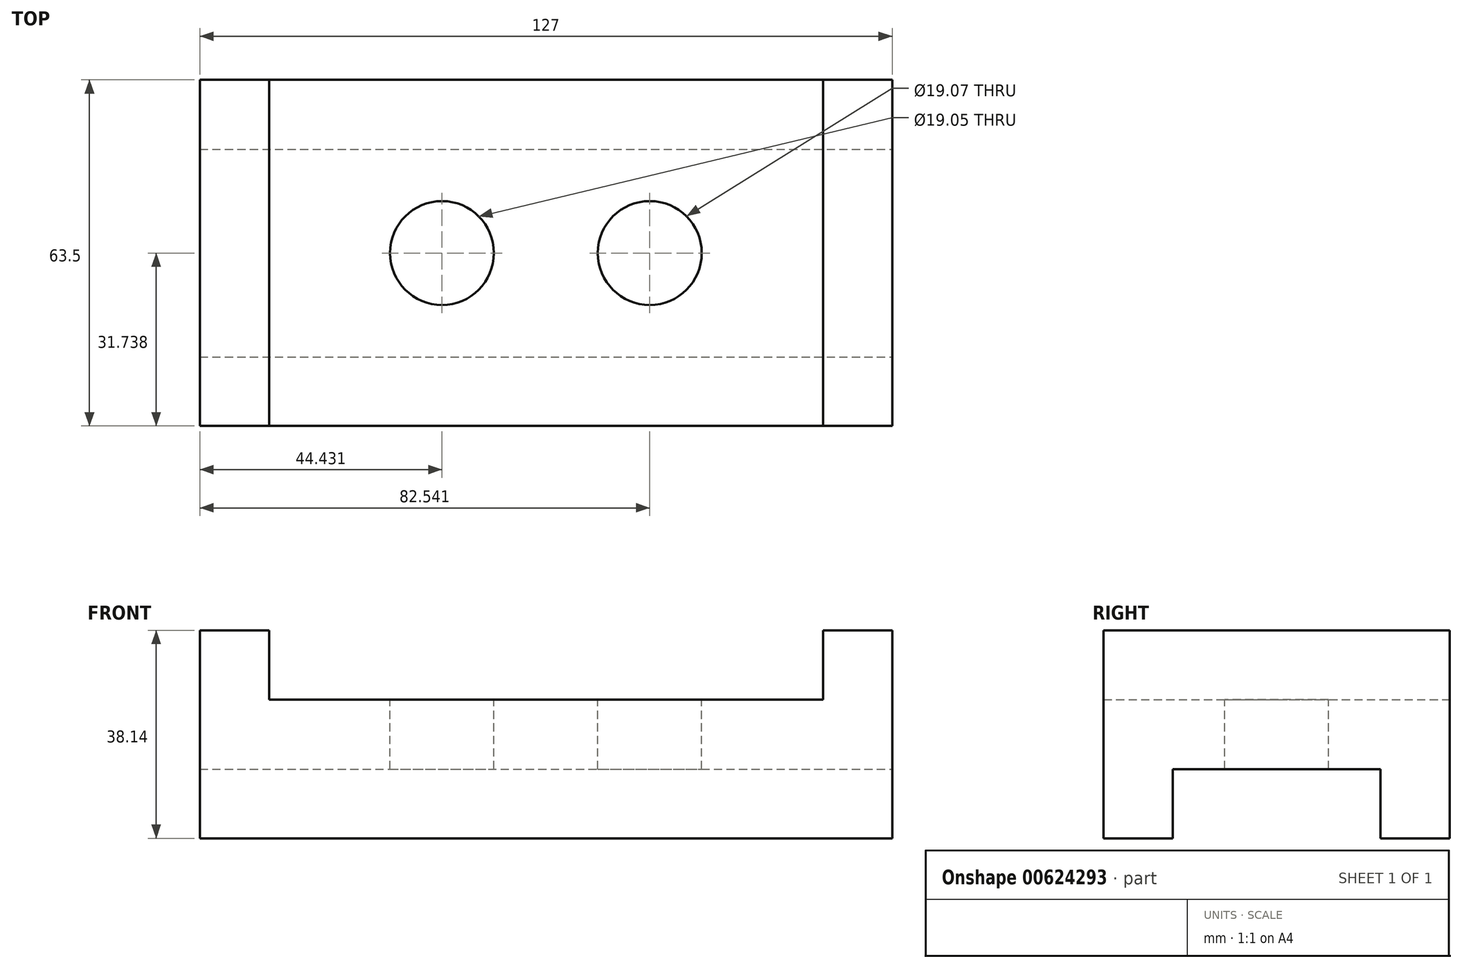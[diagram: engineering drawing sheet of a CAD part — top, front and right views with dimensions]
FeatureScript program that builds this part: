
annotation { "Feature Type Name" : "Feature", "Feature Type Description" : "" }
export const myFeature = defineFeature(function(context is Context, id is Id, definition is map)
    precondition{}
    {
        {
            var Q0;
            Q0=qCreatedBy(makeId("Front.planeOp"),FACE);
            var sketch = newSketch(context, id + "F0", { "sketchPlane" : qUnion([Q0])});
            skLineSegment(sketch, "E0", {"start": v(0, 0) * mm, "end": v(-63.5, 0) * mm});
            skLineSegment(sketch, "E1", {"start": v(-63.5, 0) * mm, "end": v(-63.5, 38.14) * mm});
            skLineSegment(sketch, "E2", {"start": v(-63.5, 38.14) * mm, "end": v(-50.8, 38.14) * mm});
            skLineSegment(sketch, "E3", {"start": v(-50.8, 38.14) * mm, "end": v(-50.8, 25.43) * mm});
            skLineSegment(sketch, "E4", {"start": v(-50.8, 25.43) * mm, "end": v(0, 25.43) * mm});
            skLineSegment(sketch, "E5.MirrorCS", {"start": v(63.5, 0) * mm, "end": v(63.5, 38.14) * mm});
            skLineSegment(sketch, "E6.MirrorCS", {"start": v(50.8, 25.43) * mm, "end": v(0, 25.43) * mm});
            skLineSegment(sketch, "E7.MirrorCS", {"start": v(0, 0) * mm, "end": v(63.5, 0) * mm});
            skLineSegment(sketch, "E8.MirrorCS", {"start": v(63.5, 38.14) * mm, "end": v(50.8, 38.14) * mm});
            skLineSegment(sketch, "E9.MirrorCS", {"start": v(50.8, 38.14) * mm, "end": v(50.8, 25.43) * mm});
            skSolve(sketch);
        }
        {
            var Q0;
            Q0=makeQuery(id+"F0.imprint","IMPRINT",FACE,{"disambiguationData":[TD([[makeQuery(id+"F0.imprint","IMPRINT",EDGE,{"derivedFrom":sQuery(id+"F0.wireOp",EDGE,"E0")}),-1.0]])]});
            extrude(context, id + "F1", {"entities" : qUnion([Q0]), "depth" : 63.5 * mm, "offsetDistance" : 25.4 * mm});
        }
        {
            var Q0;
            Q0=makeQuery(id+"F1.opExtrude","SWEPT_FACE",FACE,{"disambiguationData":[OSD([sQuery(id+"F0.wireOp",EDGE,"E5.MirrorCS")])]});
            var sketch = newSketch(context, id + "F2", { "sketchPlane" : qUnion([Q0])});
            skLineSegment(sketch, "E10", {"start": v(-50.81, 0) * mm, "end": v(-50.81, 12.7) * mm});
            skLineSegment(sketch, "E11", {"start": v(-50.81, 12.7) * mm, "end": v(-12.71, 12.7) * mm});
            skLineSegment(sketch, "E12", {"start": v(-12.71, 12.7) * mm, "end": v(-12.71, 0) * mm});
            skSolve(sketch);
        }
        {
            var Q0;
            {var subQ0=sQuery(id+"F2.wireOp",EDGE,"E10");Q0=makeQuery(id+"F2.imprint","IMPRINT",FACE,{"disambiguationData":[TD([[makeQuery(id+"F2.imprint","IMPRINT",EDGE,{"derivedFrom":subQ0}),-1.0]])]});}
            extrude(context, id + "F3", {"entities" : qUnion([Q0]), "operationType" : NewBodyOperationType.REMOVE, "oppositeDirection" : true, "depth" : 127 * mm, "offsetDistance" : 25.4 * mm});
        }
        {
            var Q0;
            Q0=makeQuery(id+"F1.opExtrude","SWEPT_FACE",FACE,{"disambiguationData":[OSD([sQuery(id+"F0.wireOp",EDGE,"E4"),sQuery(id+"F0.wireOp",EDGE,"E6.MirrorCS")])]});
            var sketch = newSketch(context, id + "F4", { "sketchPlane" : qUnion([Q0])});
            skCircle(sketch, "E13", {"center": v(-19.07, -31.76) * mm, "radius": 9.53 * mm});
            skCircle(sketch, "E14", {"center": v(19.04, -31.76) * mm, "radius": 9.53 * mm});
            skSolve(sketch);
        }
        {
            var Q0;
            Q0=makeQuery(id+"F4.imprint","IMPRINT",FACE,{"disambiguationData":[TD([[makeQuery(id+"F4.imprint","IMPRINT",EDGE,{"derivedFrom":sQuery(id+"F4.wireOp",EDGE,"E13")}),1.0]])]});
            var Q1;
            Q1=makeQuery(id+"F4.imprint","IMPRINT",FACE,{"disambiguationData":[TD([[makeQuery(id+"F4.imprint","IMPRINT",EDGE,{"derivedFrom":sQuery(id+"F4.wireOp",EDGE,"E14")}),1.0]])]});
            extrude(context, id + "F5", {"entities" : qUnion([Q0, Q1]), "operationType" : NewBodyOperationType.REMOVE, "oppositeDirection" : true, "depth" : 38.1 * mm, "offsetDistance" : 25.4 * mm});
        }
    });
